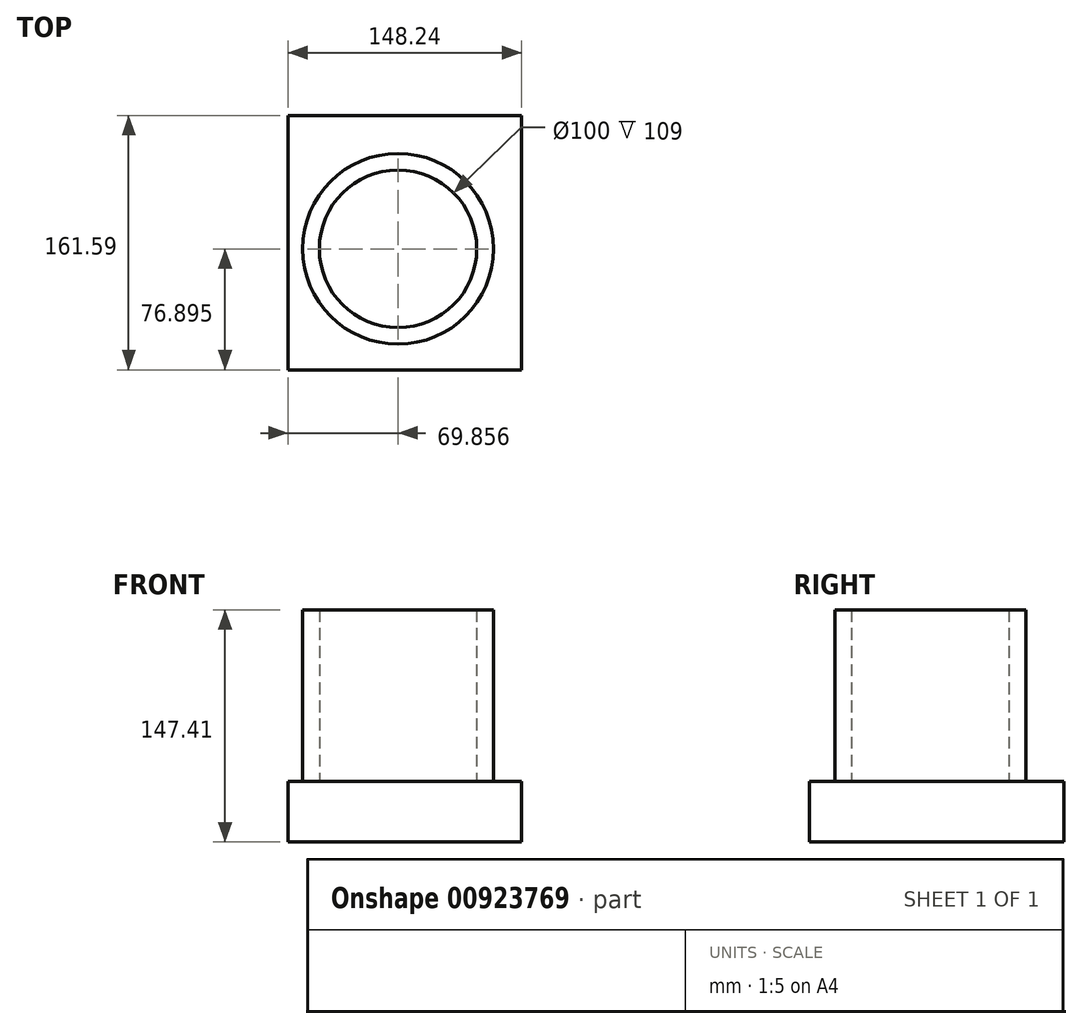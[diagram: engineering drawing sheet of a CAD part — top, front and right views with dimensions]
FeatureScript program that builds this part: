
annotation { "Feature Type Name" : "Feature", "Feature Type Description" : "" }
export const myFeature = defineFeature(function(context is Context, id is Id, definition is map)
    precondition{}
    {
        {
            var Q0;
            Q0=qCreatedBy(makeId("Top.planeOp"),FACE);
            var sketch = newSketch(context, id + "F0", { "sketchPlane" : qUnion([Q0])});
            skCircle(sketch, "E0", {"center": v(-166.33, 45.54) * mm, "radius": 50 * mm});
            skCircle(sketch, "E1", {"center": v(-166.33, 45.54) * mm, "radius": 60.57 * mm});
            skSolve(sketch);
        }
        {
            var Q0;
            Q0=makeQuery(id+"F0.imprint","IMPRINT",FACE,{"disambiguationData":[TD([[makeQuery(id+"F0.imprint","IMPRINT",EDGE,{"derivedFrom":sQuery(id+"F0.wireOp",EDGE,"E0")}),-1.0]])]});
            extrude(context, id + "F1", {"entities" : qUnion([Q0]), "depth" : 109 * mm, "offsetDistance" : 25 * mm});
        }
        {
            var Q0;
            Q0=makeQuery(id+"F1.opExtrude","CAP_FACE",FACE,{"disambiguationData":[OSD([sQuery(id+"F0.wireOp",EDGE,"E0"),sQuery(id+"F0.wireOp",EDGE,"E1")])],"isStart":true});
            var Q1;
            Q1 = qSketchRegion(id + "F0", true);
            extrude(context, id + "F2", {"entities" : qUnion([Q0, Q1]), "operationType" : NewBodyOperationType.ADD, "depth" : 25 * mm, "offsetDistance" : 25 * mm});
        }
        {
            var Q0;
            Q0=qCreatedBy(makeId("Top.planeOp"),FACE);
            var sketch = newSketch(context, id + "F3", { "sketchPlane" : qUnion([Q0])});
            skLineSegment(sketch, "E2.bottom", {"start": v(-236.19, -31.36) * mm, "end": v(-87.95, -31.36) * mm});
            skLineSegment(sketch, "E2.top", {"start": v(-236.19, 130.23) * mm, "end": v(-87.95, 130.23) * mm});
            skLineSegment(sketch, "E2.left", {"start": v(-236.19, -31.36) * mm, "end": v(-236.19, 130.23) * mm});
            skLineSegment(sketch, "E2.right", {"start": v(-87.95, -31.36) * mm, "end": v(-87.95, 130.23) * mm});
            skSolve(sketch);
        }
        {
            var Q0;
            Q0 = qSketchRegion(id + "F3", true);
            extrude(context, id + "F4", {"entities" : qUnion([Q0]), "operationType" : NewBodyOperationType.ADD, "oppositeDirection" : true, "depth" : 38.4 * mm, "offsetDistance" : 25 * mm});
        }
    });
